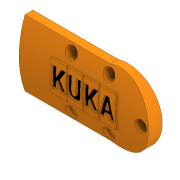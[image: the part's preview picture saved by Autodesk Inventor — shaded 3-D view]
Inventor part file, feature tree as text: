
AUTODESK INVENTOR PART (.ipt)
format: ipt  version: 2020 (Build 240168000, 168)  size: 465,408 bytes
history: native  units: in
note: dims shown in document units (in); Inventor stores cm internally (conversion verified against a paired STEP export)
features: sketch x9, extrude x8, plane x2, fillet x1, emboss x1, projected_geometry x1
ambient origin geometry x8: Origin, YZ Plane, XZ Plane, XY Plane, X Axis, Y Axis, Z Axis, Center Point
bodies: Solid1 (feature_tree)
feature tree (22):
  extrude  "Extrusion1"  Depth=0.2362in
  extrude  "Extrusion2"  Depth=0.2362in
  extrude  "Extrusion3"  Depth=0.2362in
  fillet  "Fillet1"  Radius=0.2264in
  plane  "Work Plane1"
  extrude  "Extrusion4"  Depth=0.1969in
  sketch  "Sketch5"  dims[d11=0.0in d12=0.0in d13=0.0787in]
  extrude  "Extrusion5"  Depth=0.0787in
  extrude  "Extrusion6"  Depth=0.5512in
  extrude  "Extrusion7"  Depth=0.9843in
  emboss  "Emboss1"
  plane  "Work Plane2"
  extrude  "Extrusion8"  Depth=0.0197in
  sketch  "Sketch1"  dims[d0=0.1575in d1=0.2362in]
  sketch  "Sketch2"  dims[d2=0.2362in d3=0.2362in]
  sketch  "Sketch3"  dims[d4=0.2362in d5=0.2362in d6=0.2264in d7=0.0in]
  sketch  "Sketch4"  dims[d8=0.1969in d9=0.0in d10=0.1969in]
  projected_geometry  "Projected Loop1"
  sketch  "Sketch6"  dims[d14=0.5512in d15=0.5512in]
  sketch  "Sketch7"  dims[d16=0.9843in d17=0.9843in]
  sketch  "Sketch8"  dims[d18=0.0787in d19=0.0in d20=0.0197in]
  sketch  "Sketch9"  dims[d21=0.0197in d22=0.0197in d23=0.0in d24=0.0in d25=0.0787in d26=0.0in d27=0.0in d28=0.0in d29=0.0394in d30=0.0in d31=0.3543in d32=0.3543in d33=0.3543in d34=0.3543in d35=0.3543in d36=0.4724in d37=0.0in]
